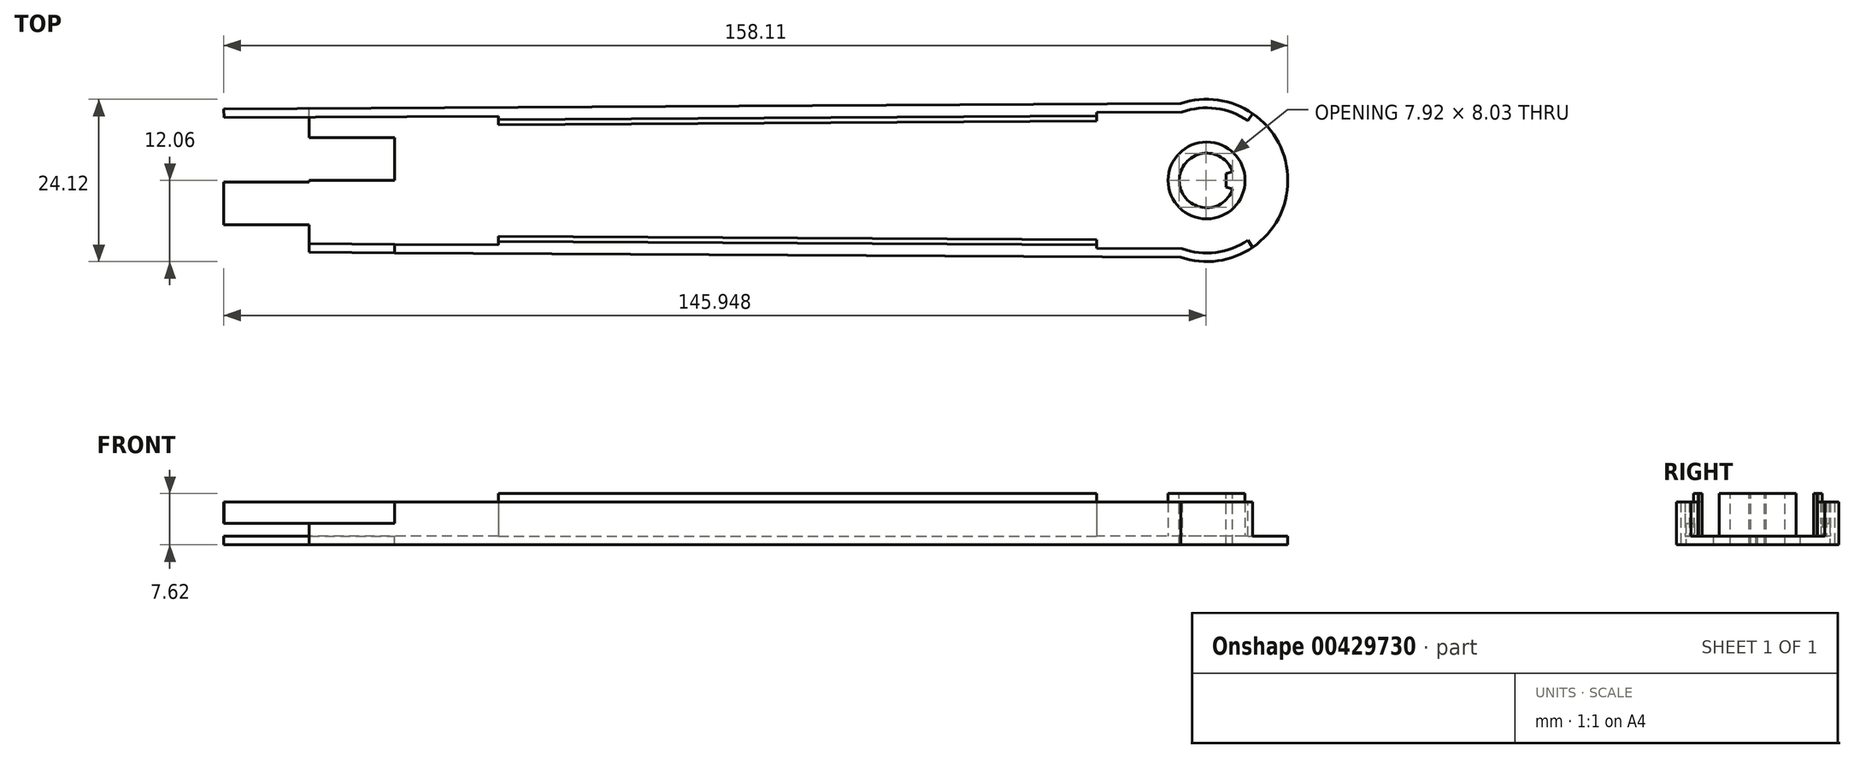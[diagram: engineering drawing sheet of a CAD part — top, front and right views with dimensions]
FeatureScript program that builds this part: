
annotation { "Feature Type Name" : "Feature", "Feature Type Description" : "" }
export const myFeature = defineFeature(function(context is Context, id is Id, definition is map)
    precondition{}
    {
        {
            var Q0;
            Q0=qCreatedBy(makeId("Top.planeOp"),FACE);
            var sketch = newSketch(context, id + "F0", { "sketchPlane" : qUnion([Q0])});
            skPoint(sketch, "E0", {"position": v(-133.35, 0) * mm});
            skPoint(sketch, "E1", {"position": v(133.35, 0) * mm});
            skCircle(sketch, "E2", {"center": v(-133.35, 0) * mm, "radius": 10.16 * mm});
            skCircle(sketch, "E3", {"center": v(133.35, 0) * mm, "radius": 12.06 * mm});
            skPoint(sketch, "E4", {"position": v(-131.1, 9.9) * mm});
            skPoint(sketch, "E5", {"position": v(-131.1, -9.9) * mm});
            skPoint(sketch, "E6", {"position": v(129.49, 11.43) * mm});
            skPoint(sketch, "E7", {"position": v(129.49, -11.43) * mm});
            skLineSegment(sketch, "E8", {"start": v(129.49, 11.43) * mm, "end": v(-131.1, 9.9) * mm});
            skLineSegment(sketch, "E9", {"start": v(129.49, -11.43) * mm, "end": v(-131.1, -9.9) * mm});
            skPoint(sketch, "E10", {"position": v(0, 31.92) * mm});
            skPoint(sketch, "E11", {"position": v(0, -28.95) * mm});
            skLineSegment(sketch, "E12", {"start": v(0, 31.92) * mm, "end": v(0, -28.95) * mm});
            skSolve(sketch);
        }
        {
            var Q0;
            {var subQ0=sQuery(id+"F0.wireOp",EDGE,"E8");var subQ1=sQuery(id+"F0.wireOp",EDGE,"E3");var subQ2=makeQuery(id+"F0.imprint","INTERSECT",VERTEX,{"derivedFrom":[subQ1,subQ0]});Q0=makeQuery(id+"F0.imprint","IMPRINT",FACE,{"disambiguationData":[TD([[makeQuery(id+"F0.imprint","IMPRINT",EDGE,{"disambiguationData":[TD([[subQ2,-1.0]])],"derivedFrom":subQ1}),-1.0]])]});}
            var Q1;
            {var subQ0=sQuery(id+"F0.wireOp",EDGE,"E3");var subQ1=makeQuery(id+"F0.imprint","INTERSECT",VERTEX,{"derivedFrom":[subQ0,sQuery(id+"F0.wireOp",EDGE,"E8")]});Q1=makeQuery(id+"F0.imprint","IMPRINT",FACE,{"disambiguationData":[TD([[makeQuery(id+"F0.imprint","IMPRINT",EDGE,{"disambiguationData":[TD([[subQ1,-1.0]])],"derivedFrom":subQ0}),1.0]])]});}
            extrude(context, id + "F1", {"entities" : qUnion([Q0, Q1]), "depth" : 6.35 * mm});
        }
        {
            var Q0;
            Q0=makeQuery(id+"F1.opExtrude","CAP_FACE",FACE,{"disambiguationData":[OSD([sQuery(id+"F0.wireOp",EDGE,"E3"),sQuery(id+"F0.wireOp",EDGE,"E8"),sQuery(id+"F0.wireOp",EDGE,"E9"),sQuery(id+"F0.wireOp",EDGE,"E12")])],"isStart":false});
            var Q1;
            Q1=makeQuery(id+"F1.opExtrude","SWEPT_FACE",FACE,{"disambiguationData":[OSD([sQuery(id+"F0.wireOp",EDGE,"E12")])]});
            shell(context, id + "F2", {"entities" : qUnion([Q0, Q1]), "thickness" : 1.27 * mm});
        }
        {
            var Q0;
            Q0=makeQuery(id+"F2.opShell","OFFSET_FACE",FACE,{"disambiguationData":[OSD([sQuery(id+"F0.wireOp",EDGE,"E3"),sQuery(id+"F0.wireOp",EDGE,"E8"),sQuery(id+"F0.wireOp",EDGE,"E9"),sQuery(id+"F0.wireOp",EDGE,"E12")])]});
            var sketch = newSketch(context, id + "F3", { "sketchPlane" : qUnion([Q0])});
            skLineSegment(sketch, "E13.bottom", {"start": v(0, 0) * mm, "end": v(12.7, 0) * mm});
            skLineSegment(sketch, "E13.top", {"start": v(0, 6.35) * mm, "end": v(12.7, 6.35) * mm});
            skLineSegment(sketch, "E13.left", {"start": v(0, 0) * mm, "end": v(0, 6.35) * mm});
            skLineSegment(sketch, "E13.right", {"start": v(12.7, 0) * mm, "end": v(12.7, 6.35) * mm});
            skSolve(sketch);
        }
        {
            var Q0;
            Q0=makeQuery(id+"F3.imprint","IMPRINT",FACE,{"disambiguationData":[TD([[makeQuery(id+"F3.imprint","IMPRINT",EDGE,{"derivedFrom":sQuery(id+"F3.wireOp",EDGE,"E13.bottom")}),1.0]])]});
            extrude(context, id + "F4", {"entities" : qUnion([Q0]), "operationType" : NewBodyOperationType.REMOVE, "oppositeDirection" : true, "depth" : 25.4 * mm});
        }
        {
            var Q0;
            Q0=makeQuery(id+"F2.opShell","OFFSET_FACE",FACE,{"disambiguationData":[OSD([sQuery(id+"F0.wireOp",EDGE,"E3"),sQuery(id+"F0.wireOp",EDGE,"E8"),sQuery(id+"F0.wireOp",EDGE,"E9"),sQuery(id+"F0.wireOp",EDGE,"E12")])]});
            var sketch = newSketch(context, id + "F5", { "sketchPlane" : qUnion([Q0])});
            skPoint(sketch, "E14", {"position": v(0, -0.25) * mm});
            skLineSegment(sketch, "E15.bottom", {"start": v(0, -0.25) * mm, "end": v(-12.7, -0.25) * mm});
            skLineSegment(sketch, "E15.top", {"start": v(0, -6.58) * mm, "end": v(-12.7, -6.58) * mm});
            skLineSegment(sketch, "E15.left", {"start": v(0, -0.25) * mm, "end": v(0, -6.58) * mm});
            skLineSegment(sketch, "E15.right", {"start": v(-12.7, -0.25) * mm, "end": v(-12.7, -6.58) * mm});
            skSolve(sketch);
        }
        {
            var Q0;
            Q0=makeQuery(id+"F5.imprint","IMPRINT",FACE,{"disambiguationData":[TD([[makeQuery(id+"F5.imprint","IMPRINT",EDGE,{"derivedFrom":sQuery(id+"F5.wireOp",EDGE,"E15.bottom")}),1.0]])]});
            extrude(context, id + "F6", {"entities" : qUnion([Q0]), "operationType" : NewBodyOperationType.ADD, "oppositeDirection" : true, "depth" : 1.27 * mm});
        }
        {
            var Q0;
            Q0=makeQuery(id+"F1.opExtrude","SWEPT_FACE",FACE,{"disambiguationData":[OSD([sQuery(id+"F0.wireOp",EDGE,"E8")])]});
            var sketch = newSketch(context, id + "F7", { "sketchPlane" : qUnion([Q0])});
            skLineSegment(sketch, "E16.bottom", {"start": v(-0.06, 6.35) * mm, "end": v(12.64, 6.35) * mm});
            skLineSegment(sketch, "E16.top", {"start": v(-0.06, 3.23) * mm, "end": v(12.64, 3.23) * mm});
            skLineSegment(sketch, "E16.left", {"start": v(-0.06, 6.35) * mm, "end": v(-0.06, 3.23) * mm});
            skLineSegment(sketch, "E16.right", {"start": v(12.64, 6.35) * mm, "end": v(12.64, 3.23) * mm});
            skSolve(sketch);
        }
        {
            var Q0;
            Q0=makeQuery(id+"F7.imprint","IMPRINT",FACE,{"disambiguationData":[TD([[makeQuery(id+"F7.imprint","IMPRINT",EDGE,{"derivedFrom":sQuery(id+"F7.wireOp",EDGE,"E16.bottom")}),-1.0]])]});
            extrude(context, id + "F8", {"entities" : qUnion([Q0]), "operationType" : NewBodyOperationType.ADD, "oppositeDirection" : true, "depth" : 1.27 * mm});
        }
        {
            var Q0;
            Q0=makeQuery(id+"F2.opShell","OFFSET_FACE",FACE,{"disambiguationData":[OSD([sQuery(id+"F0.wireOp",EDGE,"E9")])]});
            var sketch = newSketch(context, id + "F9", { "sketchPlane" : qUnion([Q0])});
            skLineSegment(sketch, "E17.bottom", {"start": v(-0.05, 6.35) * mm, "end": v(-12.75, 6.35) * mm});
            skLineSegment(sketch, "E17.top", {"start": v(-0.05, 3.18) * mm, "end": v(-12.75, 3.17) * mm});
            skLineSegment(sketch, "E17.left", {"start": v(-0.05, 6.35) * mm, "end": v(-0.05, 3.18) * mm});
            skLineSegment(sketch, "E17.right", {"start": v(-12.75, 6.35) * mm, "end": v(-12.75, 3.17) * mm});
            skSolve(sketch);
        }
        {
            var Q0;
            Q0=makeQuery(id+"F9.imprint","IMPRINT",FACE,{"disambiguationData":[TD([[makeQuery(id+"F9.imprint","IMPRINT",EDGE,{"derivedFrom":sQuery(id+"F9.wireOp",EDGE,"E17.bottom")}),-1.0]])]});
            extrude(context, id + "F10", {"entities" : qUnion([Q0]), "operationType" : NewBodyOperationType.REMOVE, "oppositeDirection" : true, "depth" : 25.4 * mm});
        }
        {
            var Q0;
            Q0=makeQuery(id+"F6.boolean.opBoolean","MERGE",FACE,{"derivedFrom":[makeQuery(id+"F2.opShell","OFFSET_FACE",FACE,{"disambiguationData":[OSD([sQuery(id+"F0.wireOp",EDGE,"E3"),sQuery(id+"F0.wireOp",EDGE,"E8"),sQuery(id+"F0.wireOp",EDGE,"E9"),sQuery(id+"F0.wireOp",EDGE,"E12")])]}),makeQuery(id+"F6.opExtrude","CAP_FACE",FACE,{"disambiguationData":[OSD([sQuery(id+"F5.wireOp",EDGE,"E15.bottom"),sQuery(id+"F5.wireOp",EDGE,"E15.top"),sQuery(id+"F5.wireOp",EDGE,"E15.left"),sQuery(id+"F5.wireOp",EDGE,"E15.right")])],"isStart":true})]});
            var sketch = newSketch(context, id + "F11", { "sketchPlane" : qUnion([Q0])});
            skLineSegment(sketch, "E18", {"start": v(117, 10.09) * mm, "end": v(28.1, 9.57) * mm});
            skLineSegment(sketch, "E19", {"start": v(28.1, 8.3) * mm, "end": v(117, 8.82) * mm});
            skLineSegment(sketch, "E20", {"start": v(28.1, 8.3) * mm, "end": v(28.1, 9.57) * mm});
            skLineSegment(sketch, "E21", {"start": v(117, 8.82) * mm, "end": v(117, 10.09) * mm});
            skLineSegment(sketch, "E22", {"start": v(117, -10.09) * mm, "end": v(28.1, -9.57) * mm});
            skLineSegment(sketch, "E23", {"start": v(28.1, -8.3) * mm, "end": v(117, -8.82) * mm});
            skLineSegment(sketch, "E24", {"start": v(28.1, -8.3) * mm, "end": v(28.1, -9.57) * mm});
            skLineSegment(sketch, "E25", {"start": v(117, -8.82) * mm, "end": v(117, -10.09) * mm});
            skSolve(sketch);
        }
        {
            var Q0;
            Q0=makeQuery(id+"F11.imprint","IMPRINT",FACE,{"disambiguationData":[TD([[makeQuery(id+"F11.imprint","IMPRINT",EDGE,{"derivedFrom":sQuery(id+"F11.wireOp",EDGE,"E18")}),1.0]])]});
            var Q1;
            Q1=makeQuery(id+"F11.imprint","IMPRINT",FACE,{"disambiguationData":[TD([[makeQuery(id+"F11.imprint","IMPRINT",EDGE,{"derivedFrom":sQuery(id+"F11.wireOp",EDGE,"E22")}),-1.0]])]});
            extrude(context, id + "F12", {"entities" : qUnion([Q0, Q1]), "operationType" : NewBodyOperationType.ADD, "depth" : 5.08 * mm});
        }
        {
            var Q0;
            Q0=makeQuery(id+"F6.boolean.opBoolean","MERGE",FACE,{"derivedFrom":[makeQuery(id+"F2.opShell","OFFSET_FACE",FACE,{"disambiguationData":[OSD([sQuery(id+"F0.wireOp",EDGE,"E3"),sQuery(id+"F0.wireOp",EDGE,"E8"),sQuery(id+"F0.wireOp",EDGE,"E9"),sQuery(id+"F0.wireOp",EDGE,"E12")])]}),makeQuery(id+"F6.opExtrude","CAP_FACE",FACE,{"disambiguationData":[OSD([sQuery(id+"F5.wireOp",EDGE,"E15.bottom"),sQuery(id+"F5.wireOp",EDGE,"E15.top"),sQuery(id+"F5.wireOp",EDGE,"E15.left"),sQuery(id+"F5.wireOp",EDGE,"E15.right")])],"isStart":true})]});
            var sketch = newSketch(context, id + "F13", { "sketchPlane" : qUnion([Q0])});
            skCircle(sketch, "E26", {"center": v(133.35, 0) * mm, "radius": 5.72 * mm});
            skSolve(sketch);
        }
        {
            var Q0;
            Q0=makeQuery(id+"F13.imprint","IMPRINT",FACE,{"disambiguationData":[TD([[makeQuery(id+"F13.imprint","IMPRINT",EDGE,{"derivedFrom":sQuery(id+"F13.wireOp",EDGE,"E26")}),1.0]])]});
            extrude(context, id + "F14", {"entities" : qUnion([Q0]), "operationType" : NewBodyOperationType.ADD, "depth" : 6.35 * mm});
        }
        {
            var Q0;
            Q0=makeQuery(id+"F14.opExtrude","CAP_FACE",FACE,{"disambiguationData":[OSD([sQuery(id+"F13.wireOp",EDGE,"E26")])],"isStart":false});
            var sketch = newSketch(context, id + "F15", { "sketchPlane" : qUnion([Q0])});
            skCircle(sketch, "E27", {"center": v(133.35, 0) * mm, "radius": 4.06 * mm});
            skPoint(sketch, "E28", {"position": v(137.21, 1.27) * mm});
            skPoint(sketch, "E29", {"position": v(137.21, -1.27) * mm});
            skPoint(sketch, "E30", {"position": v(136.25, 1.02) * mm});
            skPoint(sketch, "E31", {"position": v(136.25, -1.02) * mm});
            skLineSegment(sketch, "E32", {"start": v(137.21, 1.27) * mm, "end": v(136.25, 1.02) * mm});
            skLineSegment(sketch, "E33", {"start": v(136.25, -1.02) * mm, "end": v(136.25, 1.02) * mm});
            skLineSegment(sketch, "E34", {"start": v(137.21, -1.27) * mm, "end": v(136.25, -1.02) * mm});
            skSolve(sketch);
        }
        {
            var Q0;
            {var subQ0=sQuery(id+"F15.wireOp",EDGE,"E32");Q0=makeQuery(id+"F15.imprint","IMPRINT",FACE,{"disambiguationData":[TD([[makeQuery(id+"F15.imprint","IMPRINT",EDGE,{"derivedFrom":subQ0}),-1.0]])]});}
            extrude(context, id + "F16", {"entities" : qUnion([Q0]), "operationType" : NewBodyOperationType.REMOVE, "oppositeDirection" : true, "depth" : 25.4 * mm});
        }
        {
            var Q0;
            Q0=makeQuery(id+"F8.boolean.opBoolean","MERGE",FACE,{"derivedFrom":[makeQuery(id+"F1.opExtrude","CAP_FACE",FACE,{"disambiguationData":[OSD([sQuery(id+"F0.wireOp",EDGE,"E3"),sQuery(id+"F0.wireOp",EDGE,"E8"),sQuery(id+"F0.wireOp",EDGE,"E9"),sQuery(id+"F0.wireOp",EDGE,"E12")])],"isStart":false}),makeQuery(id+"F8.opExtrude","SWEPT_FACE",FACE,{"disambiguationData":[OSD([sQuery(id+"F7.wireOp",EDGE,"E16.bottom")])]})]});
            var sketch = newSketch(context, id + "F17", { "sketchPlane" : qUnion([Q0])});
            skPoint(sketch, "E35", {"position": v(139.47, 8.89) * mm});
            skPoint(sketch, "E36", {"position": v(139.47, -8.9) * mm});
            skPoint(sketch, "E37", {"position": v(140.2, 9.94) * mm});
            skPoint(sketch, "E38", {"position": v(140.2, -9.94) * mm});
            skPoint(sketch, "E39", {"position": v(133.35, 0) * mm});
            skLineSegment(sketch, "E40", {"start": v(133.35, 0) * mm, "end": v(140.2, 9.94) * mm});
            skLineSegment(sketch, "E41", {"start": v(140.2, -9.94) * mm, "end": v(133.35, 0) * mm});
            skArc(sketch, "E42", {"start": v(140.2, 9.94) * mm, "mid": v(145.42, 0) * mm, "end": v(140.2, -9.94) * mm});
            skArc(sketch, "E43", {"start": v(139.47, 8.89) * mm, "mid": v(144.15, 0) * mm, "end": v(139.47, -8.9) * mm});
            skSolve(sketch);
        }
        {
            var Q0;
            {var subQ0=sQuery(id+"F17.wireOp",EDGE,"E42");Q0=makeQuery(id+"F17.imprint","IMPRINT",FACE,{"disambiguationData":[TD([[makeQuery(id+"F17.imprint","IMPRINT",EDGE,{"derivedFrom":subQ0}),1.0]])]});}
            var Q1;
            Q1=makeQuery(id+"F6.boolean.opBoolean","MERGE",FACE,{"derivedFrom":[makeQuery(id+"F2.opShell","OFFSET_FACE",FACE,{"disambiguationData":[OSD([sQuery(id+"F0.wireOp",EDGE,"E3"),sQuery(id+"F0.wireOp",EDGE,"E8"),sQuery(id+"F0.wireOp",EDGE,"E9"),sQuery(id+"F0.wireOp",EDGE,"E12")])]}),makeQuery(id+"F6.opExtrude","CAP_FACE",FACE,{"disambiguationData":[OSD([sQuery(id+"F5.wireOp",EDGE,"E15.bottom"),sQuery(id+"F5.wireOp",EDGE,"E15.top"),sQuery(id+"F5.wireOp",EDGE,"E15.left"),sQuery(id+"F5.wireOp",EDGE,"E15.right")])],"isStart":true})]});
            extrude(context, id + "F18", {"entities" : qUnion([Q0]), "operationType" : NewBodyOperationType.REMOVE, "endBound" : BoundingType.UP_TO_SURFACE, "oppositeDirection" : true, "endBoundEntityFace" : qUnion([Q1]), "depth" : 25.4 * mm});
        }
        {
            var Q0;
            {var subQ0=sQuery(id+"F11.wireOp",EDGE,"E21");var subQ1=sQuery(id+"F11.wireOp",EDGE,"E20");var subQ2=sQuery(id+"F0.wireOp",EDGE,"E3");var subQ6=sQuery(id+"F7.wireOp",EDGE,"E16.bottom");var subQ7=sQuery(id+"F0.wireOp",EDGE,"E8");var subQ8=sQuery(id+"F11.wireOp",EDGE,"E19");Q0=makeQuery(id+"F18.boolean.opBoolean","SPLIT",FACE,{"disambiguationData":[TD([makeQuery(id+"F1.opExtrude","SWEPT_FACE",FACE,{"disambiguationData":[OSD([subQ7])]})])],"derivedFrom":makeQuery(id+"F12.boolean.opBoolean","MERGE",FACE,{"derivedFrom":[makeQuery(id+"F8.boolean.opBoolean","MERGE",FACE,{"derivedFrom":[makeQuery(id+"F1.opExtrude","CAP_FACE",FACE,{"disambiguationData":[OSD([subQ2,subQ7,sQuery(id+"F0.wireOp",EDGE,"E9"),sQuery(id+"F0.wireOp",EDGE,"E12")])],"isStart":false}),makeQuery(id+"F8.opExtrude","SWEPT_FACE",FACE,{"disambiguationData":[OSD([subQ6])]})]}),makeQuery(id+"F12.opExtrude","CAP_FACE",FACE,{"disambiguationData":[OSD([sQuery(id+"F11.wireOp",EDGE,"E18"),subQ8,subQ1,subQ0])],"isStart":false}),makeQuery(id+"F12.opExtrude","CAP_FACE",FACE,{"disambiguationData":[OSD([sQuery(id+"F11.wireOp",EDGE,"E22"),sQuery(id+"F11.wireOp",EDGE,"E23"),sQuery(id+"F11.wireOp",EDGE,"E24"),sQuery(id+"F11.wireOp",EDGE,"E25")])],"isStart":false})]})});}
            var sketch = newSketch(context, id + "F19", { "sketchPlane" : qUnion([Q0])});
            skLineSegment(sketch, "E44", {"start": v(28.1, 8.3) * mm, "end": v(28.1, 9.06) * mm});
            skLineSegment(sketch, "E45", {"start": v(117, 8.82) * mm, "end": v(117, 9.58) * mm});
            skLineSegment(sketch, "E46", {"start": v(117, 9.58) * mm, "end": v(28.1, 9.06) * mm});
            skLineSegment(sketch, "E47", {"start": v(28.1, 8.3) * mm, "end": v(117, 8.82) * mm});
            skLineSegment(sketch, "E48.MirrorCS", {"start": v(28.1, -8.3) * mm, "end": v(28.1, -9.06) * mm});
            skLineSegment(sketch, "E49.MirrorCS", {"start": v(117, -8.82) * mm, "end": v(117, -9.58) * mm});
            skLineSegment(sketch, "E50.MirrorCS", {"start": v(117, -9.58) * mm, "end": v(28.1, -9.06) * mm});
            skLineSegment(sketch, "E51.MirrorCS", {"start": v(28.1, -8.3) * mm, "end": v(117, -8.82) * mm});
            skSolve(sketch);
        }
        {
            var Q0;
            {var subQ0=sQuery(id+"F19.wireOp",EDGE,"E45");Q0=makeQuery(id+"F19.imprint","IMPRINT",FACE,{"disambiguationData":[TD([[makeQuery(id+"F19.imprint","IMPRINT",EDGE,{"derivedFrom":subQ0}),1.0]])]});}
            var Q1;
            Q1=makeQuery(id+"F19.imprint","IMPRINT",FACE,{"disambiguationData":[TD([[makeQuery(id+"F19.imprint","IMPRINT",EDGE,{"derivedFrom":sQuery(id+"F19.wireOp",EDGE,"E48.MirrorCS")}),1.0]])]});
            extrude(context, id + "F20", {"entities" : qUnion([Q0, Q1]), "operationType" : NewBodyOperationType.ADD, "depth" : 1.27 * mm});
        }
    });
